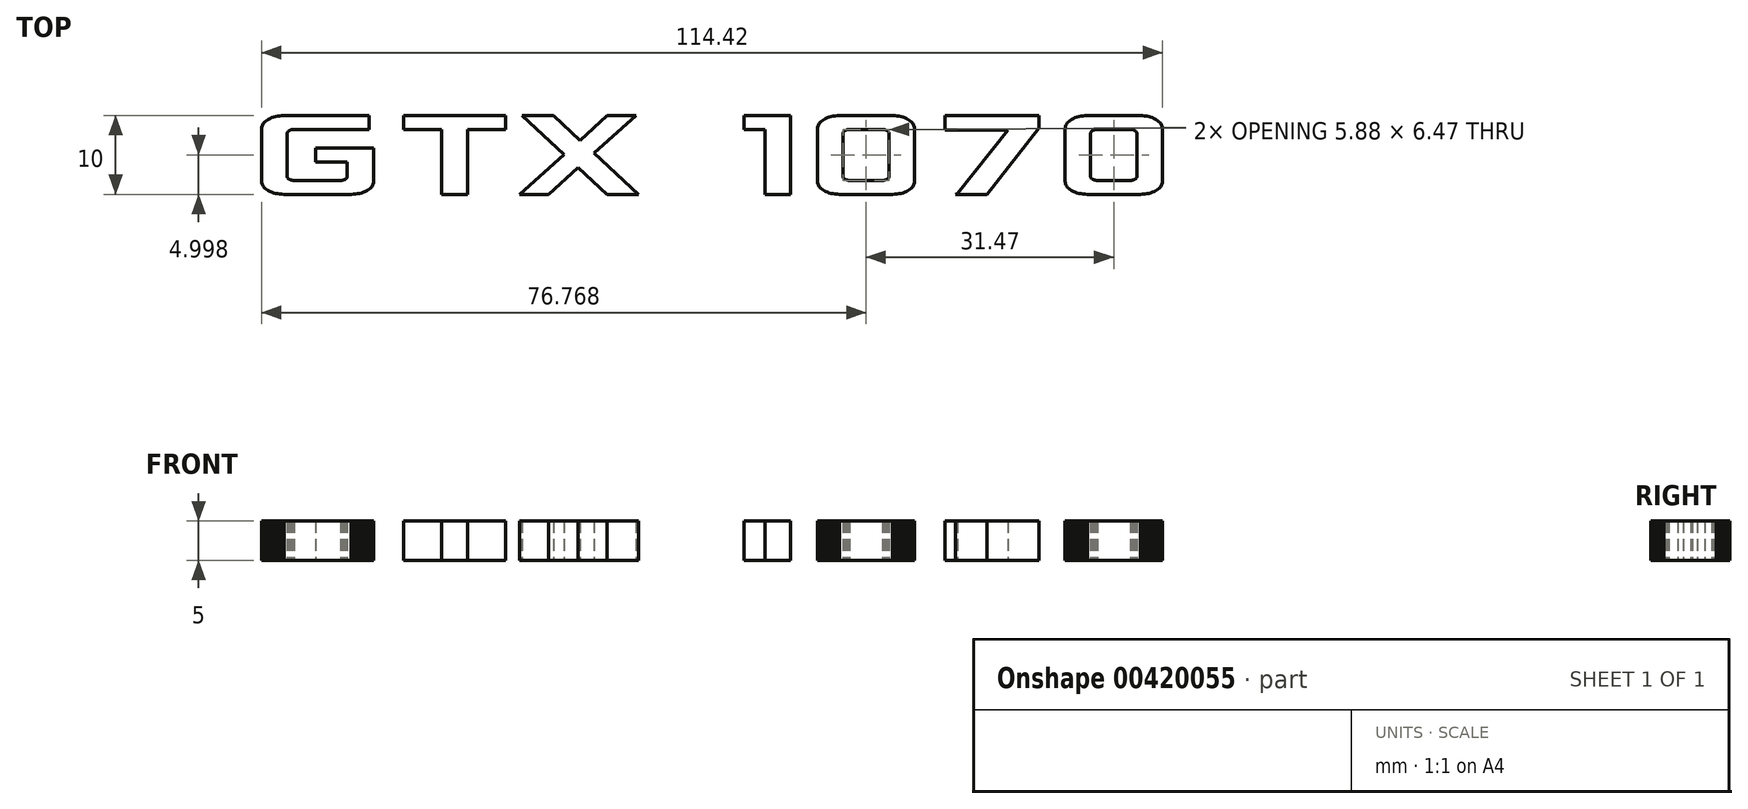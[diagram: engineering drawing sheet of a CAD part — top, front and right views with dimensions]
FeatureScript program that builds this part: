
annotation { "Feature Type Name" : "Feature", "Feature Type Description" : "" }
export const myFeature = defineFeature(function(context is Context, id is Id, definition is map)
    precondition{}
    {
        {
            var Q0;
            Q0=qCreatedBy(makeId("Top.planeOp"),FACE);
            var sketch = newSketch(context, id + "F0", { "sketchPlane" : qUnion([Q0])});
            skLineSegment(sketch, "E0", {"start": v(-58.1, -5.92) * mm, "end": v(-58.1, 0.75) * mm});
            skLineSegment(sketch, "E1", {"start": v(-58.1, 0.75) * mm, "end": v(-58.08, 0.92) * mm});
            skLineSegment(sketch, "E2", {"start": v(-58.08, 0.92) * mm, "end": v(-58.04, 1.09) * mm});
            skLineSegment(sketch, "E3", {"start": v(-58.04, 1.09) * mm, "end": v(-57.98, 1.25) * mm});
            skLineSegment(sketch, "E4", {"start": v(-57.98, 1.25) * mm, "end": v(-57.89, 1.4) * mm});
            skLineSegment(sketch, "E5", {"start": v(-57.89, 1.4) * mm, "end": v(-57.77, 1.54) * mm});
            skLineSegment(sketch, "E6", {"start": v(-57.77, 1.54) * mm, "end": v(-57.63, 1.68) * mm});
            skLineSegment(sketch, "E7", {"start": v(-57.63, 1.68) * mm, "end": v(-57.46, 1.81) * mm});
            skLineSegment(sketch, "E8", {"start": v(-57.46, 1.81) * mm, "end": v(-57.27, 1.94) * mm});
            skLineSegment(sketch, "E9", {"start": v(-57.27, 1.94) * mm, "end": v(-57.06, 2.05) * mm});
            skLineSegment(sketch, "E10", {"start": v(-57.06, 2.05) * mm, "end": v(-56.83, 2.15) * mm});
            skLineSegment(sketch, "E11", {"start": v(-56.83, 2.15) * mm, "end": v(-56.6, 2.24) * mm});
            skLineSegment(sketch, "E12", {"start": v(-56.6, 2.24) * mm, "end": v(-56.35, 2.3) * mm});
            skLineSegment(sketch, "E13", {"start": v(-56.35, 2.3) * mm, "end": v(-56.1, 2.36) * mm});
            skLineSegment(sketch, "E14", {"start": v(-56.1, 2.36) * mm, "end": v(-55.83, 2.4) * mm});
            skLineSegment(sketch, "E15", {"start": v(-55.83, 2.4) * mm, "end": v(-55.55, 2.42) * mm});
            skLineSegment(sketch, "E16", {"start": v(-55.55, 2.42) * mm, "end": v(-55.26, 2.43) * mm});
            skLineSegment(sketch, "E17", {"start": v(-55.26, 2.43) * mm, "end": v(-44.47, 2.43) * mm});
            skLineSegment(sketch, "E18", {"start": v(-44.47, 2.43) * mm, "end": v(-44.47, 0.66) * mm});
            skLineSegment(sketch, "E19", {"start": v(-44.47, 0.66) * mm, "end": v(-54, 0.66) * mm});
            skLineSegment(sketch, "E20", {"start": v(-54, 0.66) * mm, "end": v(-54.1, 0.66) * mm});
            skLineSegment(sketch, "E21", {"start": v(-54.1, 0.66) * mm, "end": v(-54.17, 0.65) * mm});
            skLineSegment(sketch, "E22", {"start": v(-54.17, 0.65) * mm, "end": v(-54.26, 0.64) * mm});
            skLineSegment(sketch, "E23", {"start": v(-54.26, 0.64) * mm, "end": v(-54.33, 0.63) * mm});
            skLineSegment(sketch, "E24", {"start": v(-54.33, 0.63) * mm, "end": v(-54.4, 0.6) * mm});
            skLineSegment(sketch, "E25", {"start": v(-54.4, 0.6) * mm, "end": v(-54.48, 0.58) * mm});
            skLineSegment(sketch, "E26", {"start": v(-54.48, 0.58) * mm, "end": v(-54.55, 0.55) * mm});
            skLineSegment(sketch, "E27", {"start": v(-54.55, 0.55) * mm, "end": v(-54.61, 0.51) * mm});
            skLineSegment(sketch, "E28", {"start": v(-54.61, 0.51) * mm, "end": v(-54.67, 0.47) * mm});
            skLineSegment(sketch, "E29", {"start": v(-54.67, 0.47) * mm, "end": v(-54.72, 0.43) * mm});
            skLineSegment(sketch, "E30", {"start": v(-54.72, 0.43) * mm, "end": v(-54.76, 0.4) * mm});
            skLineSegment(sketch, "E31", {"start": v(-54.76, 0.4) * mm, "end": v(-54.8, 0.35) * mm});
            skLineSegment(sketch, "E32", {"start": v(-54.8, 0.35) * mm, "end": v(-54.83, 0.3) * mm});
            skLineSegment(sketch, "E33", {"start": v(-54.83, 0.3) * mm, "end": v(-54.85, 0.26) * mm});
            skLineSegment(sketch, "E34", {"start": v(-54.85, 0.26) * mm, "end": v(-54.86, 0.2) * mm});
            skLineSegment(sketch, "E35", {"start": v(-54.86, 0.2) * mm, "end": v(-54.86, 0.16) * mm});
            skLineSegment(sketch, "E36", {"start": v(-54.86, 0.16) * mm, "end": v(-54.86, -5.31) * mm});
            skLineSegment(sketch, "E37", {"start": v(-54.86, -5.31) * mm, "end": v(-54.86, -5.36) * mm});
            skLineSegment(sketch, "E38", {"start": v(-54.86, -5.36) * mm, "end": v(-54.85, -5.41) * mm});
            skLineSegment(sketch, "E39", {"start": v(-54.85, -5.41) * mm, "end": v(-54.83, -5.46) * mm});
            skLineSegment(sketch, "E40", {"start": v(-54.83, -5.46) * mm, "end": v(-54.8, -5.5) * mm});
            skLineSegment(sketch, "E41", {"start": v(-54.8, -5.5) * mm, "end": v(-54.76, -5.55) * mm});
            skLineSegment(sketch, "E42", {"start": v(-54.76, -5.55) * mm, "end": v(-54.72, -5.59) * mm});
            skLineSegment(sketch, "E43", {"start": v(-54.72, -5.59) * mm, "end": v(-54.67, -5.63) * mm});
            skLineSegment(sketch, "E44", {"start": v(-54.67, -5.63) * mm, "end": v(-54.6, -5.66) * mm});
            skLineSegment(sketch, "E45", {"start": v(-54.6, -5.66) * mm, "end": v(-54.54, -5.7) * mm});
            skLineSegment(sketch, "E46", {"start": v(-54.54, -5.7) * mm, "end": v(-54.48, -5.73) * mm});
            skLineSegment(sketch, "E47", {"start": v(-54.48, -5.73) * mm, "end": v(-54.4, -5.75) * mm});
            skLineSegment(sketch, "E48", {"start": v(-54.4, -5.75) * mm, "end": v(-54.33, -5.77) * mm});
            skLineSegment(sketch, "E49", {"start": v(-54.33, -5.77) * mm, "end": v(-54.25, -5.79) * mm});
            skLineSegment(sketch, "E50", {"start": v(-54.25, -5.79) * mm, "end": v(-54.17, -5.8) * mm});
            skLineSegment(sketch, "E51", {"start": v(-54.17, -5.8) * mm, "end": v(-54.09, -5.8) * mm});
            skLineSegment(sketch, "E52", {"start": v(-54.09, -5.8) * mm, "end": v(-54, -5.8) * mm});
            skLineSegment(sketch, "E53", {"start": v(-54, -5.8) * mm, "end": v(-48.07, -5.8) * mm});
            skLineSegment(sketch, "E54", {"start": v(-48.07, -5.8) * mm, "end": v(-47.99, -5.8) * mm});
            skLineSegment(sketch, "E55", {"start": v(-47.99, -5.8) * mm, "end": v(-47.9, -5.8) * mm});
            skLineSegment(sketch, "E56", {"start": v(-47.9, -5.8) * mm, "end": v(-47.82, -5.79) * mm});
            skLineSegment(sketch, "E57", {"start": v(-47.82, -5.79) * mm, "end": v(-47.74, -5.77) * mm});
            skLineSegment(sketch, "E58", {"start": v(-47.74, -5.77) * mm, "end": v(-47.67, -5.75) * mm});
            skLineSegment(sketch, "E59", {"start": v(-47.67, -5.75) * mm, "end": v(-47.6, -5.73) * mm});
            skLineSegment(sketch, "E60", {"start": v(-47.6, -5.73) * mm, "end": v(-47.53, -5.7) * mm});
            skLineSegment(sketch, "E61", {"start": v(-47.53, -5.7) * mm, "end": v(-47.47, -5.67) * mm});
            skLineSegment(sketch, "E62", {"start": v(-47.47, -5.67) * mm, "end": v(-47.4, -5.63) * mm});
            skLineSegment(sketch, "E63", {"start": v(-47.4, -5.63) * mm, "end": v(-47.36, -5.59) * mm});
            skLineSegment(sketch, "E64", {"start": v(-47.36, -5.59) * mm, "end": v(-47.31, -5.55) * mm});
            skLineSegment(sketch, "E65", {"start": v(-47.31, -5.55) * mm, "end": v(-47.28, -5.5) * mm});
            skLineSegment(sketch, "E66", {"start": v(-47.28, -5.5) * mm, "end": v(-47.25, -5.46) * mm});
            skLineSegment(sketch, "E67", {"start": v(-47.25, -5.46) * mm, "end": v(-47.23, -5.42) * mm});
            skLineSegment(sketch, "E68", {"start": v(-47.23, -5.42) * mm, "end": v(-47.22, -5.37) * mm});
            skLineSegment(sketch, "E69", {"start": v(-47.22, -5.37) * mm, "end": v(-47.21, -5.32) * mm});
            skLineSegment(sketch, "E70", {"start": v(-47.21, -5.32) * mm, "end": v(-47.21, -3.45) * mm});
            skLineSegment(sketch, "E71", {"start": v(-47.21, -3.45) * mm, "end": v(-51.23, -3.45) * mm});
            skLineSegment(sketch, "E72", {"start": v(-51.23, -3.45) * mm, "end": v(-51.23, -1.7) * mm});
            skLineSegment(sketch, "E73", {"start": v(-51.23, -1.7) * mm, "end": v(-43.88, -1.7) * mm});
            skLineSegment(sketch, "E74", {"start": v(-43.88, -1.7) * mm, "end": v(-43.88, -5.93) * mm});
            skLineSegment(sketch, "E75", {"start": v(-43.88, -5.93) * mm, "end": v(-43.9, -6.1) * mm});
            skLineSegment(sketch, "E76", {"start": v(-43.9, -6.1) * mm, "end": v(-43.93, -6.25) * mm});
            skLineSegment(sketch, "E77", {"start": v(-43.93, -6.25) * mm, "end": v(-44, -6.4) * mm});
            skLineSegment(sketch, "E78", {"start": v(-44, -6.4) * mm, "end": v(-44.09, -6.55) * mm});
            skLineSegment(sketch, "E79", {"start": v(-44.09, -6.55) * mm, "end": v(-44.2, -6.7) * mm});
            skLineSegment(sketch, "E80", {"start": v(-44.2, -6.7) * mm, "end": v(-44.35, -6.83) * mm});
            skLineSegment(sketch, "E81", {"start": v(-44.35, -6.83) * mm, "end": v(-44.52, -6.96) * mm});
            skLineSegment(sketch, "E82", {"start": v(-44.52, -6.96) * mm, "end": v(-44.72, -7.09) * mm});
            skLineSegment(sketch, "E83", {"start": v(-44.72, -7.09) * mm, "end": v(-44.93, -7.2) * mm});
            skLineSegment(sketch, "E84", {"start": v(-44.93, -7.2) * mm, "end": v(-45.16, -7.3) * mm});
            skLineSegment(sketch, "E85", {"start": v(-45.16, -7.3) * mm, "end": v(-45.4, -7.38) * mm});
            skLineSegment(sketch, "E86", {"start": v(-45.4, -7.38) * mm, "end": v(-45.64, -7.45) * mm});
            skLineSegment(sketch, "E87", {"start": v(-45.64, -7.45) * mm, "end": v(-45.9, -7.5) * mm});
            skLineSegment(sketch, "E88", {"start": v(-45.9, -7.5) * mm, "end": v(-46.17, -7.54) * mm});
            skLineSegment(sketch, "E89", {"start": v(-46.17, -7.54) * mm, "end": v(-46.45, -7.56) * mm});
            skLineSegment(sketch, "E90", {"start": v(-46.45, -7.56) * mm, "end": v(-46.74, -7.57) * mm});
            skLineSegment(sketch, "E91", {"start": v(-46.74, -7.57) * mm, "end": v(-55.25, -7.57) * mm});
            skLineSegment(sketch, "E92", {"start": v(-55.25, -7.57) * mm, "end": v(-55.54, -7.56) * mm});
            skLineSegment(sketch, "E93", {"start": v(-55.54, -7.56) * mm, "end": v(-55.82, -7.54) * mm});
            skLineSegment(sketch, "E94", {"start": v(-55.82, -7.54) * mm, "end": v(-56.1, -7.5) * mm});
            skLineSegment(sketch, "E95", {"start": v(-56.1, -7.5) * mm, "end": v(-56.35, -7.45) * mm});
            skLineSegment(sketch, "E96", {"start": v(-56.35, -7.45) * mm, "end": v(-56.6, -7.38) * mm});
            skLineSegment(sketch, "E97", {"start": v(-56.6, -7.38) * mm, "end": v(-56.83, -7.3) * mm});
            skLineSegment(sketch, "E98", {"start": v(-56.83, -7.3) * mm, "end": v(-57.05, -7.2) * mm});
            skLineSegment(sketch, "E99", {"start": v(-57.05, -7.2) * mm, "end": v(-57.27, -7.09) * mm});
            skLineSegment(sketch, "E100", {"start": v(-57.27, -7.09) * mm, "end": v(-57.46, -6.96) * mm});
            skLineSegment(sketch, "E101", {"start": v(-57.46, -6.96) * mm, "end": v(-57.63, -6.83) * mm});
            skLineSegment(sketch, "E102", {"start": v(-57.63, -6.83) * mm, "end": v(-57.77, -6.7) * mm});
            skLineSegment(sketch, "E103", {"start": v(-57.77, -6.7) * mm, "end": v(-57.89, -6.55) * mm});
            skLineSegment(sketch, "E104", {"start": v(-57.89, -6.55) * mm, "end": v(-57.98, -6.4) * mm});
            skLineSegment(sketch, "E105", {"start": v(-57.98, -6.4) * mm, "end": v(-58.04, -6.25) * mm});
            skLineSegment(sketch, "E106", {"start": v(-58.04, -6.25) * mm, "end": v(-58.08, -6.09) * mm});
            skLineSegment(sketch, "E107", {"start": v(-58.08, -6.09) * mm, "end": v(-58.1, -5.92) * mm});
            skLineSegment(sketch, "E108", {"start": v(-40.06, 0.66) * mm, "end": v(-40.06, 2.43) * mm});
            skLineSegment(sketch, "E109", {"start": v(-40.06, 2.43) * mm, "end": v(-27.12, 2.43) * mm});
            skLineSegment(sketch, "E110", {"start": v(-27.12, 2.43) * mm, "end": v(-27.12, 0.66) * mm});
            skLineSegment(sketch, "E111", {"start": v(-27.12, 0.66) * mm, "end": v(-31.92, 0.66) * mm});
            skLineSegment(sketch, "E112", {"start": v(-31.92, 0.66) * mm, "end": v(-31.92, -7.57) * mm});
            skLineSegment(sketch, "E113", {"start": v(-31.92, -7.57) * mm, "end": v(-35.25, -7.57) * mm});
            skLineSegment(sketch, "E114", {"start": v(-35.25, -7.57) * mm, "end": v(-35.25, 0.66) * mm});
            skLineSegment(sketch, "E115", {"start": v(-35.25, 0.66) * mm, "end": v(-40.06, 0.66) * mm});
            skLineSegment(sketch, "E116", {"start": v(-25.33, -7.57) * mm, "end": v(-19.68, -2.53) * mm});
            skLineSegment(sketch, "E117", {"start": v(-19.68, -2.53) * mm, "end": v(-25, 2.43) * mm});
            skLineSegment(sketch, "E118", {"start": v(-25, 2.43) * mm, "end": v(-21, 2.43) * mm});
            skLineSegment(sketch, "E119", {"start": v(-21, 2.43) * mm, "end": v(-17.62, -0.72) * mm});
            skLineSegment(sketch, "E120", {"start": v(-17.62, -0.72) * mm, "end": v(-14.2, 2.43) * mm});
            skLineSegment(sketch, "E121", {"start": v(-14.2, 2.43) * mm, "end": v(-10.52, 2.43) * mm});
            skLineSegment(sketch, "E122", {"start": v(-10.52, 2.43) * mm, "end": v(-15.9, -2.32) * mm});
            skLineSegment(sketch, "E123", {"start": v(-15.9, -2.32) * mm, "end": v(-10.23, -7.57) * mm});
            skLineSegment(sketch, "E124", {"start": v(-10.23, -7.57) * mm, "end": v(-14.22, -7.57) * mm});
            skLineSegment(sketch, "E125", {"start": v(-14.22, -7.57) * mm, "end": v(-17.93, -4.16) * mm});
            skLineSegment(sketch, "E126", {"start": v(-17.93, -4.16) * mm, "end": v(-21.68, -7.57) * mm});
            skLineSegment(sketch, "E127", {"start": v(-21.68, -7.57) * mm, "end": v(-25.33, -7.57) * mm});
            skLineSegment(sketch, "E128", {"start": v(3.18, 0.66) * mm, "end": v(3.18, 2.43) * mm});
            skLineSegment(sketch, "E129", {"start": v(3.18, 2.43) * mm, "end": v(9.06, 2.43) * mm});
            skLineSegment(sketch, "E130", {"start": v(9.06, 2.43) * mm, "end": v(9.06, -7.57) * mm});
            skLineSegment(sketch, "E131", {"start": v(9.06, -7.57) * mm, "end": v(5.82, -7.57) * mm});
            skLineSegment(sketch, "E132", {"start": v(5.82, -7.57) * mm, "end": v(5.82, 0.66) * mm});
            skLineSegment(sketch, "E133", {"start": v(5.82, 0.66) * mm, "end": v(3.18, 0.66) * mm});
            skLineSegment(sketch, "E134", {"start": v(12.5, -5.92) * mm, "end": v(12.5, 0.75) * mm});
            skLineSegment(sketch, "E135", {"start": v(12.5, 0.75) * mm, "end": v(12.5, 0.92) * mm});
            skLineSegment(sketch, "E136", {"start": v(12.5, 0.92) * mm, "end": v(12.54, 1.09) * mm});
            skLineSegment(sketch, "E137", {"start": v(12.54, 1.09) * mm, "end": v(12.6, 1.25) * mm});
            skLineSegment(sketch, "E138", {"start": v(12.6, 1.25) * mm, "end": v(12.7, 1.4) * mm});
            skLineSegment(sketch, "E139", {"start": v(12.7, 1.4) * mm, "end": v(12.81, 1.54) * mm});
            skLineSegment(sketch, "E140", {"start": v(12.81, 1.54) * mm, "end": v(12.96, 1.68) * mm});
            skLineSegment(sketch, "E141", {"start": v(12.96, 1.68) * mm, "end": v(13.12, 1.81) * mm});
            skLineSegment(sketch, "E142", {"start": v(13.12, 1.81) * mm, "end": v(13.32, 1.94) * mm});
            skLineSegment(sketch, "E143", {"start": v(13.32, 1.94) * mm, "end": v(13.53, 2.05) * mm});
            skLineSegment(sketch, "E144", {"start": v(13.53, 2.05) * mm, "end": v(13.75, 2.15) * mm});
            skLineSegment(sketch, "E145", {"start": v(13.75, 2.15) * mm, "end": v(13.99, 2.24) * mm});
            skLineSegment(sketch, "E146", {"start": v(13.99, 2.24) * mm, "end": v(14.23, 2.3) * mm});
            skLineSegment(sketch, "E147", {"start": v(14.23, 2.3) * mm, "end": v(14.49, 2.36) * mm});
            skLineSegment(sketch, "E148", {"start": v(14.49, 2.36) * mm, "end": v(14.75, 2.4) * mm});
            skLineSegment(sketch, "E149", {"start": v(14.75, 2.4) * mm, "end": v(15.03, 2.42) * mm});
            skLineSegment(sketch, "E150", {"start": v(15.03, 2.42) * mm, "end": v(15.32, 2.43) * mm});
            skLineSegment(sketch, "E151", {"start": v(15.32, 2.43) * mm, "end": v(22.04, 2.43) * mm});
            skLineSegment(sketch, "E152", {"start": v(22.04, 2.43) * mm, "end": v(22.32, 2.42) * mm});
            skLineSegment(sketch, "E153", {"start": v(22.32, 2.42) * mm, "end": v(22.6, 2.4) * mm});
            skLineSegment(sketch, "E154", {"start": v(22.6, 2.4) * mm, "end": v(22.86, 2.36) * mm});
            skLineSegment(sketch, "E155", {"start": v(22.86, 2.36) * mm, "end": v(23.11, 2.3) * mm});
            skLineSegment(sketch, "E156", {"start": v(23.11, 2.3) * mm, "end": v(23.35, 2.24) * mm});
            skLineSegment(sketch, "E157", {"start": v(23.35, 2.24) * mm, "end": v(23.59, 2.15) * mm});
            skLineSegment(sketch, "E158", {"start": v(23.59, 2.15) * mm, "end": v(23.8, 2.05) * mm});
            skLineSegment(sketch, "E159", {"start": v(23.8, 2.05) * mm, "end": v(24.02, 1.94) * mm});
            skLineSegment(sketch, "E160", {"start": v(24.02, 1.94) * mm, "end": v(24.21, 1.81) * mm});
            skLineSegment(sketch, "E161", {"start": v(24.21, 1.81) * mm, "end": v(24.38, 1.68) * mm});
            skLineSegment(sketch, "E162", {"start": v(24.38, 1.68) * mm, "end": v(24.52, 1.54) * mm});
            skLineSegment(sketch, "E163", {"start": v(24.52, 1.54) * mm, "end": v(24.64, 1.4) * mm});
            skLineSegment(sketch, "E164", {"start": v(24.64, 1.4) * mm, "end": v(24.73, 1.25) * mm});
            skLineSegment(sketch, "E165", {"start": v(24.73, 1.25) * mm, "end": v(24.8, 1.09) * mm});
            skLineSegment(sketch, "E166", {"start": v(24.8, 1.09) * mm, "end": v(24.83, 0.92) * mm});
            skLineSegment(sketch, "E167", {"start": v(24.83, 0.92) * mm, "end": v(24.84, 0.75) * mm});
            skLineSegment(sketch, "E168", {"start": v(24.84, 0.75) * mm, "end": v(24.84, -5.92) * mm});
            skLineSegment(sketch, "E169", {"start": v(24.84, -5.92) * mm, "end": v(24.83, -6.09) * mm});
            skLineSegment(sketch, "E170", {"start": v(24.83, -6.09) * mm, "end": v(24.8, -6.25) * mm});
            skLineSegment(sketch, "E171", {"start": v(24.8, -6.25) * mm, "end": v(24.73, -6.4) * mm});
            skLineSegment(sketch, "E172", {"start": v(24.73, -6.4) * mm, "end": v(24.64, -6.56) * mm});
            skLineSegment(sketch, "E173", {"start": v(24.64, -6.56) * mm, "end": v(24.52, -6.7) * mm});
            skLineSegment(sketch, "E174", {"start": v(24.52, -6.7) * mm, "end": v(24.38, -6.83) * mm});
            skLineSegment(sketch, "E175", {"start": v(24.38, -6.83) * mm, "end": v(24.22, -6.97) * mm});
            skLineSegment(sketch, "E176", {"start": v(24.22, -6.97) * mm, "end": v(24.03, -7.09) * mm});
            skLineSegment(sketch, "E177", {"start": v(24.03, -7.09) * mm, "end": v(23.81, -7.2) * mm});
            skLineSegment(sketch, "E178", {"start": v(23.81, -7.2) * mm, "end": v(23.6, -7.3) * mm});
            skLineSegment(sketch, "E179", {"start": v(23.6, -7.3) * mm, "end": v(23.36, -7.38) * mm});
            skLineSegment(sketch, "E180", {"start": v(23.36, -7.38) * mm, "end": v(23.12, -7.45) * mm});
            skLineSegment(sketch, "E181", {"start": v(23.12, -7.45) * mm, "end": v(22.86, -7.5) * mm});
            skLineSegment(sketch, "E182", {"start": v(22.86, -7.5) * mm, "end": v(22.6, -7.54) * mm});
            skLineSegment(sketch, "E183", {"start": v(22.6, -7.54) * mm, "end": v(22.32, -7.56) * mm});
            skLineSegment(sketch, "E184", {"start": v(22.32, -7.56) * mm, "end": v(22.04, -7.57) * mm});
            skLineSegment(sketch, "E185", {"start": v(22.04, -7.57) * mm, "end": v(15.32, -7.57) * mm});
            skLineSegment(sketch, "E186", {"start": v(15.32, -7.57) * mm, "end": v(15.03, -7.56) * mm});
            skLineSegment(sketch, "E187", {"start": v(15.03, -7.56) * mm, "end": v(14.75, -7.54) * mm});
            skLineSegment(sketch, "E188", {"start": v(14.75, -7.54) * mm, "end": v(14.49, -7.5) * mm});
            skLineSegment(sketch, "E189", {"start": v(14.49, -7.5) * mm, "end": v(14.23, -7.45) * mm});
            skLineSegment(sketch, "E190", {"start": v(14.23, -7.45) * mm, "end": v(13.99, -7.39) * mm});
            skLineSegment(sketch, "E191", {"start": v(13.99, -7.39) * mm, "end": v(13.75, -7.3) * mm});
            skLineSegment(sketch, "E192", {"start": v(13.75, -7.3) * mm, "end": v(13.53, -7.2) * mm});
            skLineSegment(sketch, "E193", {"start": v(13.53, -7.2) * mm, "end": v(13.32, -7.1) * mm});
            skLineSegment(sketch, "E194", {"start": v(13.32, -7.1) * mm, "end": v(13.12, -6.97) * mm});
            skLineSegment(sketch, "E195", {"start": v(13.12, -6.97) * mm, "end": v(12.96, -6.84) * mm});
            skLineSegment(sketch, "E196", {"start": v(12.96, -6.84) * mm, "end": v(12.81, -6.7) * mm});
            skLineSegment(sketch, "E197", {"start": v(12.81, -6.7) * mm, "end": v(12.7, -6.56) * mm});
            skLineSegment(sketch, "E198", {"start": v(12.7, -6.56) * mm, "end": v(12.6, -6.4) * mm});
            skLineSegment(sketch, "E199", {"start": v(12.6, -6.4) * mm, "end": v(12.54, -6.25) * mm});
            skLineSegment(sketch, "E200", {"start": v(12.54, -6.25) * mm, "end": v(12.5, -6.09) * mm});
            skLineSegment(sketch, "E201", {"start": v(12.5, -6.09) * mm, "end": v(12.5, -5.92) * mm});
            skLineSegment(sketch, "E202", {"start": v(15.73, -5.31) * mm, "end": v(15.73, -5.36) * mm});
            skLineSegment(sketch, "E203", {"start": v(15.73, -5.36) * mm, "end": v(15.74, -5.41) * mm});
            skLineSegment(sketch, "E204", {"start": v(15.74, -5.41) * mm, "end": v(15.76, -5.46) * mm});
            skLineSegment(sketch, "E205", {"start": v(15.76, -5.46) * mm, "end": v(15.8, -5.5) * mm});
            skLineSegment(sketch, "E206", {"start": v(15.8, -5.5) * mm, "end": v(15.83, -5.55) * mm});
            skLineSegment(sketch, "E207", {"start": v(15.83, -5.55) * mm, "end": v(15.87, -5.59) * mm});
            skLineSegment(sketch, "E208", {"start": v(15.87, -5.59) * mm, "end": v(15.93, -5.63) * mm});
            skLineSegment(sketch, "E209", {"start": v(15.93, -5.63) * mm, "end": v(15.99, -5.66) * mm});
            skLineSegment(sketch, "E210", {"start": v(15.99, -5.66) * mm, "end": v(16.05, -5.7) * mm});
            skLineSegment(sketch, "E211", {"start": v(16.05, -5.7) * mm, "end": v(16.12, -5.73) * mm});
            skLineSegment(sketch, "E212", {"start": v(16.12, -5.73) * mm, "end": v(16.2, -5.75) * mm});
            skLineSegment(sketch, "E213", {"start": v(16.2, -5.75) * mm, "end": v(16.27, -5.77) * mm});
            skLineSegment(sketch, "E214", {"start": v(16.27, -5.77) * mm, "end": v(16.34, -5.79) * mm});
            skLineSegment(sketch, "E215", {"start": v(16.34, -5.79) * mm, "end": v(16.42, -5.8) * mm});
            skLineSegment(sketch, "E216", {"start": v(16.42, -5.8) * mm, "end": v(16.5, -5.8) * mm});
            skLineSegment(sketch, "E217", {"start": v(16.5, -5.8) * mm, "end": v(16.6, -5.8) * mm});
            skLineSegment(sketch, "E218", {"start": v(16.6, -5.8) * mm, "end": v(20.76, -5.8) * mm});
            skLineSegment(sketch, "E219", {"start": v(20.76, -5.8) * mm, "end": v(20.85, -5.8) * mm});
            skLineSegment(sketch, "E220", {"start": v(20.85, -5.8) * mm, "end": v(20.93, -5.8) * mm});
            skLineSegment(sketch, "E221", {"start": v(20.93, -5.8) * mm, "end": v(21.01, -5.79) * mm});
            skLineSegment(sketch, "E222", {"start": v(21.01, -5.79) * mm, "end": v(21.09, -5.77) * mm});
            skLineSegment(sketch, "E223", {"start": v(21.09, -5.77) * mm, "end": v(21.16, -5.75) * mm});
            skLineSegment(sketch, "E224", {"start": v(21.16, -5.75) * mm, "end": v(21.23, -5.73) * mm});
            skLineSegment(sketch, "E225", {"start": v(21.23, -5.73) * mm, "end": v(21.3, -5.7) * mm});
            skLineSegment(sketch, "E226", {"start": v(21.3, -5.7) * mm, "end": v(21.36, -5.66) * mm});
            skLineSegment(sketch, "E227", {"start": v(21.36, -5.66) * mm, "end": v(21.42, -5.63) * mm});
            skLineSegment(sketch, "E228", {"start": v(21.42, -5.63) * mm, "end": v(21.47, -5.59) * mm});
            skLineSegment(sketch, "E229", {"start": v(21.47, -5.59) * mm, "end": v(21.51, -5.55) * mm});
            skLineSegment(sketch, "E230", {"start": v(21.51, -5.55) * mm, "end": v(21.55, -5.5) * mm});
            skLineSegment(sketch, "E231", {"start": v(21.55, -5.5) * mm, "end": v(21.57, -5.46) * mm});
            skLineSegment(sketch, "E232", {"start": v(21.57, -5.46) * mm, "end": v(21.6, -5.41) * mm});
            skLineSegment(sketch, "E233", {"start": v(21.6, -5.41) * mm, "end": v(21.6, -5.36) * mm});
            skLineSegment(sketch, "E234", {"start": v(21.6, -5.36) * mm, "end": v(21.6, -5.31) * mm});
            skLineSegment(sketch, "E235", {"start": v(21.6, -5.31) * mm, "end": v(21.6, 0.16) * mm});
            skLineSegment(sketch, "E236", {"start": v(21.6, 0.16) * mm, "end": v(21.6, 0.2) * mm});
            skLineSegment(sketch, "E237", {"start": v(21.6, 0.2) * mm, "end": v(21.6, 0.26) * mm});
            skLineSegment(sketch, "E238", {"start": v(21.6, 0.26) * mm, "end": v(21.57, 0.3) * mm});
            skLineSegment(sketch, "E239", {"start": v(21.57, 0.3) * mm, "end": v(21.55, 0.35) * mm});
            skLineSegment(sketch, "E240", {"start": v(21.55, 0.35) * mm, "end": v(21.51, 0.4) * mm});
            skLineSegment(sketch, "E241", {"start": v(21.51, 0.4) * mm, "end": v(21.47, 0.43) * mm});
            skLineSegment(sketch, "E242", {"start": v(21.47, 0.43) * mm, "end": v(21.42, 0.47) * mm});
            skLineSegment(sketch, "E243", {"start": v(21.42, 0.47) * mm, "end": v(21.36, 0.51) * mm});
            skLineSegment(sketch, "E244", {"start": v(21.36, 0.51) * mm, "end": v(21.3, 0.55) * mm});
            skLineSegment(sketch, "E245", {"start": v(21.3, 0.55) * mm, "end": v(21.23, 0.58) * mm});
            skLineSegment(sketch, "E246", {"start": v(21.23, 0.58) * mm, "end": v(21.16, 0.6) * mm});
            skLineSegment(sketch, "E247", {"start": v(21.16, 0.6) * mm, "end": v(21.09, 0.63) * mm});
            skLineSegment(sketch, "E248", {"start": v(21.09, 0.63) * mm, "end": v(21.01, 0.64) * mm});
            skLineSegment(sketch, "E249", {"start": v(21.01, 0.64) * mm, "end": v(20.93, 0.65) * mm});
            skLineSegment(sketch, "E250", {"start": v(20.93, 0.65) * mm, "end": v(20.85, 0.66) * mm});
            skLineSegment(sketch, "E251", {"start": v(20.85, 0.66) * mm, "end": v(20.76, 0.66) * mm});
            skLineSegment(sketch, "E252", {"start": v(20.76, 0.66) * mm, "end": v(16.6, 0.66) * mm});
            skLineSegment(sketch, "E253", {"start": v(16.6, 0.66) * mm, "end": v(16.5, 0.66) * mm});
            skLineSegment(sketch, "E254", {"start": v(16.5, 0.66) * mm, "end": v(16.42, 0.65) * mm});
            skLineSegment(sketch, "E255", {"start": v(16.42, 0.65) * mm, "end": v(16.34, 0.64) * mm});
            skLineSegment(sketch, "E256", {"start": v(16.34, 0.64) * mm, "end": v(16.27, 0.63) * mm});
            skLineSegment(sketch, "E257", {"start": v(16.27, 0.63) * mm, "end": v(16.2, 0.6) * mm});
            skLineSegment(sketch, "E258", {"start": v(16.2, 0.6) * mm, "end": v(16.12, 0.58) * mm});
            skLineSegment(sketch, "E259", {"start": v(16.12, 0.58) * mm, "end": v(16.05, 0.55) * mm});
            skLineSegment(sketch, "E260", {"start": v(16.05, 0.55) * mm, "end": v(15.99, 0.51) * mm});
            skLineSegment(sketch, "E261", {"start": v(15.99, 0.51) * mm, "end": v(15.93, 0.47) * mm});
            skLineSegment(sketch, "E262", {"start": v(15.93, 0.47) * mm, "end": v(15.87, 0.43) * mm});
            skLineSegment(sketch, "E263", {"start": v(15.87, 0.43) * mm, "end": v(15.83, 0.4) * mm});
            skLineSegment(sketch, "E264", {"start": v(15.83, 0.4) * mm, "end": v(15.8, 0.35) * mm});
            skLineSegment(sketch, "E265", {"start": v(15.8, 0.35) * mm, "end": v(15.76, 0.3) * mm});
            skLineSegment(sketch, "E266", {"start": v(15.76, 0.3) * mm, "end": v(15.74, 0.26) * mm});
            skLineSegment(sketch, "E267", {"start": v(15.74, 0.26) * mm, "end": v(15.73, 0.2) * mm});
            skLineSegment(sketch, "E268", {"start": v(15.73, 0.2) * mm, "end": v(15.73, 0.16) * mm});
            skLineSegment(sketch, "E269", {"start": v(15.73, 0.16) * mm, "end": v(15.73, -5.31) * mm});
            skLineSegment(sketch, "E270", {"start": v(28.69, 0.56) * mm, "end": v(28.69, 2.43) * mm});
            skLineSegment(sketch, "E271", {"start": v(28.69, 2.43) * mm, "end": v(40.62, 2.43) * mm});
            skLineSegment(sketch, "E272", {"start": v(40.62, 2.43) * mm, "end": v(40.62, 0.86) * mm});
            skLineSegment(sketch, "E273", {"start": v(40.62, 0.86) * mm, "end": v(34.01, -7.57) * mm});
            skLineSegment(sketch, "E274", {"start": v(34.01, -7.57) * mm, "end": v(30.04, -7.57) * mm});
            skLineSegment(sketch, "E275", {"start": v(30.04, -7.57) * mm, "end": v(30.29, -7.47) * mm});
            skLineSegment(sketch, "E276", {"start": v(30.29, -7.47) * mm, "end": v(36.73, 0.56) * mm});
            skLineSegment(sketch, "E277", {"start": v(36.73, 0.56) * mm, "end": v(28.69, 0.56) * mm});
            skLineSegment(sketch, "E278", {"start": v(43.96, -5.92) * mm, "end": v(43.96, 0.75) * mm});
            skLineSegment(sketch, "E279", {"start": v(43.96, 0.75) * mm, "end": v(43.98, 0.92) * mm});
            skLineSegment(sketch, "E280", {"start": v(43.98, 0.92) * mm, "end": v(44.01, 1.09) * mm});
            skLineSegment(sketch, "E281", {"start": v(44.01, 1.09) * mm, "end": v(44.08, 1.25) * mm});
            skLineSegment(sketch, "E282", {"start": v(44.08, 1.25) * mm, "end": v(44.17, 1.4) * mm});
            skLineSegment(sketch, "E283", {"start": v(44.17, 1.4) * mm, "end": v(44.28, 1.54) * mm});
            skLineSegment(sketch, "E284", {"start": v(44.28, 1.54) * mm, "end": v(44.43, 1.68) * mm});
            skLineSegment(sketch, "E285", {"start": v(44.43, 1.68) * mm, "end": v(44.6, 1.81) * mm});
            skLineSegment(sketch, "E286", {"start": v(44.6, 1.81) * mm, "end": v(44.79, 1.94) * mm});
            skLineSegment(sketch, "E287", {"start": v(44.79, 1.94) * mm, "end": v(45, 2.05) * mm});
            skLineSegment(sketch, "E288", {"start": v(45, 2.05) * mm, "end": v(45.22, 2.15) * mm});
            skLineSegment(sketch, "E289", {"start": v(45.22, 2.15) * mm, "end": v(45.46, 2.24) * mm});
            skLineSegment(sketch, "E290", {"start": v(45.46, 2.24) * mm, "end": v(45.7, 2.3) * mm});
            skLineSegment(sketch, "E291", {"start": v(45.7, 2.3) * mm, "end": v(45.96, 2.36) * mm});
            skLineSegment(sketch, "E292", {"start": v(45.96, 2.36) * mm, "end": v(46.23, 2.4) * mm});
            skLineSegment(sketch, "E293", {"start": v(46.23, 2.4) * mm, "end": v(46.5, 2.42) * mm});
            skLineSegment(sketch, "E294", {"start": v(46.5, 2.42) * mm, "end": v(46.8, 2.43) * mm});
            skLineSegment(sketch, "E295", {"start": v(46.8, 2.43) * mm, "end": v(53.5, 2.43) * mm});
            skLineSegment(sketch, "E296", {"start": v(53.5, 2.43) * mm, "end": v(53.8, 2.42) * mm});
            skLineSegment(sketch, "E297", {"start": v(53.8, 2.42) * mm, "end": v(54.07, 2.4) * mm});
            skLineSegment(sketch, "E298", {"start": v(54.07, 2.4) * mm, "end": v(54.33, 2.36) * mm});
            skLineSegment(sketch, "E299", {"start": v(54.33, 2.36) * mm, "end": v(54.58, 2.3) * mm});
            skLineSegment(sketch, "E300", {"start": v(54.58, 2.3) * mm, "end": v(54.82, 2.24) * mm});
            skLineSegment(sketch, "E301", {"start": v(54.82, 2.24) * mm, "end": v(55.06, 2.15) * mm});
            skLineSegment(sketch, "E302", {"start": v(55.06, 2.15) * mm, "end": v(55.28, 2.05) * mm});
            skLineSegment(sketch, "E303", {"start": v(55.28, 2.05) * mm, "end": v(55.49, 1.94) * mm});
            skLineSegment(sketch, "E304", {"start": v(55.49, 1.94) * mm, "end": v(55.68, 1.81) * mm});
            skLineSegment(sketch, "E305", {"start": v(55.68, 1.81) * mm, "end": v(55.85, 1.68) * mm});
            skLineSegment(sketch, "E306", {"start": v(55.85, 1.68) * mm, "end": v(56, 1.54) * mm});
            skLineSegment(sketch, "E307", {"start": v(56, 1.54) * mm, "end": v(56.1, 1.4) * mm});
            skLineSegment(sketch, "E308", {"start": v(56.1, 1.4) * mm, "end": v(56.2, 1.25) * mm});
            skLineSegment(sketch, "E309", {"start": v(56.2, 1.25) * mm, "end": v(56.26, 1.09) * mm});
            skLineSegment(sketch, "E310", {"start": v(56.26, 1.09) * mm, "end": v(56.3, 0.92) * mm});
            skLineSegment(sketch, "E311", {"start": v(56.3, 0.92) * mm, "end": v(56.32, 0.75) * mm});
            skLineSegment(sketch, "E312", {"start": v(56.32, 0.75) * mm, "end": v(56.32, -5.92) * mm});
            skLineSegment(sketch, "E313", {"start": v(56.32, -5.92) * mm, "end": v(56.3, -6.09) * mm});
            skLineSegment(sketch, "E314", {"start": v(56.3, -6.09) * mm, "end": v(56.26, -6.25) * mm});
            skLineSegment(sketch, "E315", {"start": v(56.26, -6.25) * mm, "end": v(56.2, -6.4) * mm});
            skLineSegment(sketch, "E316", {"start": v(56.2, -6.4) * mm, "end": v(56.11, -6.56) * mm});
            skLineSegment(sketch, "E317", {"start": v(56.11, -6.56) * mm, "end": v(56, -6.7) * mm});
            skLineSegment(sketch, "E318", {"start": v(56, -6.7) * mm, "end": v(55.85, -6.83) * mm});
            skLineSegment(sketch, "E319", {"start": v(55.85, -6.83) * mm, "end": v(55.69, -6.97) * mm});
            skLineSegment(sketch, "E320", {"start": v(55.69, -6.97) * mm, "end": v(55.5, -7.09) * mm});
            skLineSegment(sketch, "E321", {"start": v(55.5, -7.09) * mm, "end": v(55.29, -7.2) * mm});
            skLineSegment(sketch, "E322", {"start": v(55.29, -7.2) * mm, "end": v(55.06, -7.3) * mm});
            skLineSegment(sketch, "E323", {"start": v(55.06, -7.3) * mm, "end": v(54.83, -7.38) * mm});
            skLineSegment(sketch, "E324", {"start": v(54.83, -7.38) * mm, "end": v(54.59, -7.45) * mm});
            skLineSegment(sketch, "E325", {"start": v(54.59, -7.45) * mm, "end": v(54.34, -7.5) * mm});
            skLineSegment(sketch, "E326", {"start": v(54.34, -7.5) * mm, "end": v(54.07, -7.54) * mm});
            skLineSegment(sketch, "E327", {"start": v(54.07, -7.54) * mm, "end": v(53.8, -7.56) * mm});
            skLineSegment(sketch, "E328", {"start": v(53.8, -7.56) * mm, "end": v(53.5, -7.57) * mm});
            skLineSegment(sketch, "E329", {"start": v(53.5, -7.57) * mm, "end": v(46.8, -7.57) * mm});
            skLineSegment(sketch, "E330", {"start": v(46.8, -7.57) * mm, "end": v(46.5, -7.56) * mm});
            skLineSegment(sketch, "E331", {"start": v(46.5, -7.56) * mm, "end": v(46.23, -7.54) * mm});
            skLineSegment(sketch, "E332", {"start": v(46.23, -7.54) * mm, "end": v(45.96, -7.5) * mm});
            skLineSegment(sketch, "E333", {"start": v(45.96, -7.5) * mm, "end": v(45.7, -7.45) * mm});
            skLineSegment(sketch, "E334", {"start": v(45.7, -7.45) * mm, "end": v(45.46, -7.39) * mm});
            skLineSegment(sketch, "E335", {"start": v(45.46, -7.39) * mm, "end": v(45.22, -7.3) * mm});
            skLineSegment(sketch, "E336", {"start": v(45.22, -7.3) * mm, "end": v(45, -7.2) * mm});
            skLineSegment(sketch, "E337", {"start": v(45, -7.2) * mm, "end": v(44.79, -7.1) * mm});
            skLineSegment(sketch, "E338", {"start": v(44.79, -7.1) * mm, "end": v(44.6, -6.97) * mm});
            skLineSegment(sketch, "E339", {"start": v(44.6, -6.97) * mm, "end": v(44.43, -6.84) * mm});
            skLineSegment(sketch, "E340", {"start": v(44.43, -6.84) * mm, "end": v(44.28, -6.7) * mm});
            skLineSegment(sketch, "E341", {"start": v(44.28, -6.7) * mm, "end": v(44.17, -6.56) * mm});
            skLineSegment(sketch, "E342", {"start": v(44.17, -6.56) * mm, "end": v(44.08, -6.4) * mm});
            skLineSegment(sketch, "E343", {"start": v(44.08, -6.4) * mm, "end": v(44.01, -6.25) * mm});
            skLineSegment(sketch, "E344", {"start": v(44.01, -6.25) * mm, "end": v(43.98, -6.09) * mm});
            skLineSegment(sketch, "E345", {"start": v(43.98, -6.09) * mm, "end": v(43.96, -5.92) * mm});
            skLineSegment(sketch, "E346", {"start": v(47.2, -5.31) * mm, "end": v(47.2, -5.36) * mm});
            skLineSegment(sketch, "E347", {"start": v(47.2, -5.36) * mm, "end": v(47.21, -5.41) * mm});
            skLineSegment(sketch, "E348", {"start": v(47.21, -5.41) * mm, "end": v(47.23, -5.46) * mm});
            skLineSegment(sketch, "E349", {"start": v(47.23, -5.46) * mm, "end": v(47.26, -5.5) * mm});
            skLineSegment(sketch, "E350", {"start": v(47.26, -5.5) * mm, "end": v(47.3, -5.55) * mm});
            skLineSegment(sketch, "E351", {"start": v(47.3, -5.55) * mm, "end": v(47.34, -5.59) * mm});
            skLineSegment(sketch, "E352", {"start": v(47.34, -5.59) * mm, "end": v(47.4, -5.63) * mm});
            skLineSegment(sketch, "E353", {"start": v(47.4, -5.63) * mm, "end": v(47.46, -5.66) * mm});
            skLineSegment(sketch, "E354", {"start": v(47.46, -5.66) * mm, "end": v(47.52, -5.7) * mm});
            skLineSegment(sketch, "E355", {"start": v(47.52, -5.7) * mm, "end": v(47.6, -5.73) * mm});
            skLineSegment(sketch, "E356", {"start": v(47.6, -5.73) * mm, "end": v(47.66, -5.75) * mm});
            skLineSegment(sketch, "E357", {"start": v(47.66, -5.75) * mm, "end": v(47.74, -5.77) * mm});
            skLineSegment(sketch, "E358", {"start": v(47.74, -5.77) * mm, "end": v(47.81, -5.79) * mm});
            skLineSegment(sketch, "E359", {"start": v(47.81, -5.79) * mm, "end": v(47.9, -5.8) * mm});
            skLineSegment(sketch, "E360", {"start": v(47.9, -5.8) * mm, "end": v(47.98, -5.8) * mm});
            skLineSegment(sketch, "E361", {"start": v(47.98, -5.8) * mm, "end": v(48.06, -5.8) * mm});
            skLineSegment(sketch, "E362", {"start": v(48.06, -5.8) * mm, "end": v(52.23, -5.8) * mm});
            skLineSegment(sketch, "E363", {"start": v(52.23, -5.8) * mm, "end": v(52.32, -5.8) * mm});
            skLineSegment(sketch, "E364", {"start": v(52.32, -5.8) * mm, "end": v(52.4, -5.8) * mm});
            skLineSegment(sketch, "E365", {"start": v(52.4, -5.8) * mm, "end": v(52.48, -5.79) * mm});
            skLineSegment(sketch, "E366", {"start": v(52.48, -5.79) * mm, "end": v(52.56, -5.77) * mm});
            skLineSegment(sketch, "E367", {"start": v(52.56, -5.77) * mm, "end": v(52.63, -5.75) * mm});
            skLineSegment(sketch, "E368", {"start": v(52.63, -5.75) * mm, "end": v(52.7, -5.73) * mm});
            skLineSegment(sketch, "E369", {"start": v(52.7, -5.73) * mm, "end": v(52.77, -5.7) * mm});
            skLineSegment(sketch, "E370", {"start": v(52.77, -5.7) * mm, "end": v(52.83, -5.66) * mm});
            skLineSegment(sketch, "E371", {"start": v(52.83, -5.66) * mm, "end": v(52.9, -5.63) * mm});
            skLineSegment(sketch, "E372", {"start": v(52.9, -5.63) * mm, "end": v(52.94, -5.59) * mm});
            skLineSegment(sketch, "E373", {"start": v(52.94, -5.59) * mm, "end": v(52.98, -5.55) * mm});
            skLineSegment(sketch, "E374", {"start": v(52.98, -5.55) * mm, "end": v(53.02, -5.5) * mm});
            skLineSegment(sketch, "E375", {"start": v(53.02, -5.5) * mm, "end": v(53.05, -5.46) * mm});
            skLineSegment(sketch, "E376", {"start": v(53.05, -5.46) * mm, "end": v(53.06, -5.41) * mm});
            skLineSegment(sketch, "E377", {"start": v(53.06, -5.41) * mm, "end": v(53.08, -5.36) * mm});
            skLineSegment(sketch, "E378", {"start": v(53.08, -5.36) * mm, "end": v(53.08, -5.31) * mm});
            skLineSegment(sketch, "E379", {"start": v(53.08, -5.31) * mm, "end": v(53.08, 0.16) * mm});
            skLineSegment(sketch, "E380", {"start": v(53.08, 0.16) * mm, "end": v(53.08, 0.2) * mm});
            skLineSegment(sketch, "E381", {"start": v(53.08, 0.2) * mm, "end": v(53.06, 0.26) * mm});
            skLineSegment(sketch, "E382", {"start": v(53.06, 0.26) * mm, "end": v(53.05, 0.3) * mm});
            skLineSegment(sketch, "E383", {"start": v(53.05, 0.3) * mm, "end": v(53.02, 0.35) * mm});
            skLineSegment(sketch, "E384", {"start": v(53.02, 0.35) * mm, "end": v(52.98, 0.4) * mm});
            skLineSegment(sketch, "E385", {"start": v(52.98, 0.4) * mm, "end": v(52.94, 0.43) * mm});
            skLineSegment(sketch, "E386", {"start": v(52.94, 0.43) * mm, "end": v(52.9, 0.47) * mm});
            skLineSegment(sketch, "E387", {"start": v(52.9, 0.47) * mm, "end": v(52.83, 0.51) * mm});
            skLineSegment(sketch, "E388", {"start": v(52.83, 0.51) * mm, "end": v(52.77, 0.55) * mm});
            skLineSegment(sketch, "E389", {"start": v(52.77, 0.55) * mm, "end": v(52.7, 0.58) * mm});
            skLineSegment(sketch, "E390", {"start": v(52.7, 0.58) * mm, "end": v(52.63, 0.6) * mm});
            skLineSegment(sketch, "E391", {"start": v(52.63, 0.6) * mm, "end": v(52.56, 0.63) * mm});
            skLineSegment(sketch, "E392", {"start": v(52.56, 0.63) * mm, "end": v(52.48, 0.64) * mm});
            skLineSegment(sketch, "E393", {"start": v(52.48, 0.64) * mm, "end": v(52.4, 0.65) * mm});
            skLineSegment(sketch, "E394", {"start": v(52.4, 0.65) * mm, "end": v(52.32, 0.66) * mm});
            skLineSegment(sketch, "E395", {"start": v(52.32, 0.66) * mm, "end": v(52.23, 0.66) * mm});
            skLineSegment(sketch, "E396", {"start": v(52.23, 0.66) * mm, "end": v(48.06, 0.66) * mm});
            skLineSegment(sketch, "E397", {"start": v(48.06, 0.66) * mm, "end": v(47.98, 0.66) * mm});
            skLineSegment(sketch, "E398", {"start": v(47.98, 0.66) * mm, "end": v(47.9, 0.65) * mm});
            skLineSegment(sketch, "E399", {"start": v(47.9, 0.65) * mm, "end": v(47.81, 0.64) * mm});
            skLineSegment(sketch, "E400", {"start": v(47.81, 0.64) * mm, "end": v(47.74, 0.63) * mm});
            skLineSegment(sketch, "E401", {"start": v(47.74, 0.63) * mm, "end": v(47.66, 0.6) * mm});
            skLineSegment(sketch, "E402", {"start": v(47.66, 0.6) * mm, "end": v(47.6, 0.58) * mm});
            skLineSegment(sketch, "E403", {"start": v(47.6, 0.58) * mm, "end": v(47.52, 0.55) * mm});
            skLineSegment(sketch, "E404", {"start": v(47.52, 0.55) * mm, "end": v(47.46, 0.51) * mm});
            skLineSegment(sketch, "E405", {"start": v(47.46, 0.51) * mm, "end": v(47.4, 0.47) * mm});
            skLineSegment(sketch, "E406", {"start": v(47.4, 0.47) * mm, "end": v(47.34, 0.43) * mm});
            skLineSegment(sketch, "E407", {"start": v(47.34, 0.43) * mm, "end": v(47.3, 0.4) * mm});
            skLineSegment(sketch, "E408", {"start": v(47.3, 0.4) * mm, "end": v(47.26, 0.35) * mm});
            skLineSegment(sketch, "E409", {"start": v(47.26, 0.35) * mm, "end": v(47.23, 0.3) * mm});
            skLineSegment(sketch, "E410", {"start": v(47.23, 0.3) * mm, "end": v(47.21, 0.26) * mm});
            skLineSegment(sketch, "E411", {"start": v(47.21, 0.26) * mm, "end": v(47.2, 0.2) * mm});
            skLineSegment(sketch, "E412", {"start": v(47.2, 0.2) * mm, "end": v(47.2, 0.16) * mm});
            skLineSegment(sketch, "E413", {"start": v(47.2, 0.16) * mm, "end": v(47.2, -5.31) * mm});
            skSolve(sketch);
        }
        {
            var Q0;
            Q0=makeQuery(id+"F0.imprint","IMPRINT",FACE,{"disambiguationData":[TD([[makeQuery(id+"F0.imprint","IMPRINT",EDGE,{"derivedFrom":sQuery(id+"F0.wireOp",EDGE,"E0")}),-1.0]])]});
            var Q1;
            Q1=makeQuery(id+"F0.imprint","IMPRINT",FACE,{"disambiguationData":[TD([[makeQuery(id+"F0.imprint","IMPRINT",EDGE,{"derivedFrom":sQuery(id+"F0.wireOp",EDGE,"E108")}),-1.0]])]});
            var Q2;
            Q2=makeQuery(id+"F0.imprint","IMPRINT",FACE,{"disambiguationData":[TD([[makeQuery(id+"F0.imprint","IMPRINT",EDGE,{"derivedFrom":sQuery(id+"F0.wireOp",EDGE,"E116")}),-1.0]])]});
            var Q3;
            Q3=makeQuery(id+"F0.imprint","IMPRINT",FACE,{"disambiguationData":[TD([[makeQuery(id+"F0.imprint","IMPRINT",EDGE,{"derivedFrom":sQuery(id+"F0.wireOp",EDGE,"E128")}),-1.0]])]});
            var Q4;
            Q4=makeQuery(id+"F0.imprint","IMPRINT",FACE,{"disambiguationData":[TD([[makeQuery(id+"F0.imprint","IMPRINT",EDGE,{"derivedFrom":sQuery(id+"F0.wireOp",EDGE,"E270")}),-1.0]])]});
            var Q5;
            Q5=makeQuery(id+"F0.imprint","IMPRINT",FACE,{"disambiguationData":[TD([[makeQuery(id+"F0.imprint","IMPRINT",EDGE,{"derivedFrom":sQuery(id+"F0.wireOp",EDGE,"E134")}),-1.0]])]});
            var Q6;
            Q6=makeQuery(id+"F0.imprint","IMPRINT",FACE,{"disambiguationData":[TD([[makeQuery(id+"F0.imprint","IMPRINT",EDGE,{"derivedFrom":sQuery(id+"F0.wireOp",EDGE,"E278")}),-1.0]])]});
            extrude(context, id + "F1", {"entities" : qUnion([Q0, Q1, Q2, Q3, Q4, Q5, Q6]), "depth" : 5 * mm});
        }
    });
